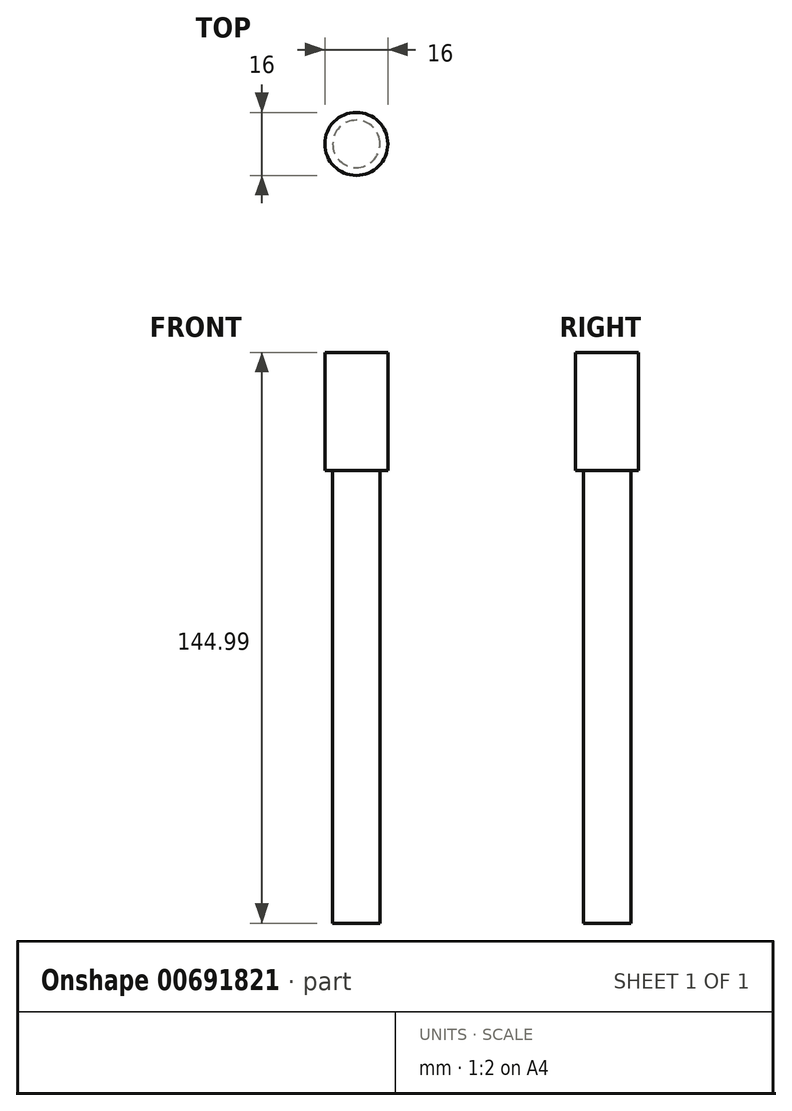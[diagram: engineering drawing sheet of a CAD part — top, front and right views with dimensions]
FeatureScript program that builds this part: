
annotation { "Feature Type Name" : "Feature", "Feature Type Description" : "" }
export const myFeature = defineFeature(function(context is Context, id is Id, definition is map)
    precondition{}
    {
        {
            var Q0;
            Q0=qCreatedBy(makeId("Front.planeOp"),FACE);
            var sketch = newSketch(context, id + "F0", { "sketchPlane" : qUnion([Q0])});
            skLineSegment(sketch, "E0.bottom", {"start": v(6, -72.5) * mm, "end": v(-6, -72.5) * mm});
            skLineSegment(sketch, "E0.top", {"start": v(6, 72.5) * mm, "end": v(-6, 72.5) * mm});
            skLineSegment(sketch, "E0.left", {"start": v(6, -72.5) * mm, "end": v(6, 72.5) * mm});
            skLineSegment(sketch, "E0.right", {"start": v(-6, -72.5) * mm, "end": v(-6, 72.5) * mm});
            skPoint(sketch, "E0.middle", {"position": v(0, 0) * mm});
            skLineSegment(sketch, "E1.bottom", {"start": v(8, 42.5) * mm, "end": v(-8, 42.5) * mm});
            skLineSegment(sketch, "E1.top", {"start": v(8, 72.5) * mm, "end": v(-8, 72.5) * mm});
            skLineSegment(sketch, "E1.left", {"start": v(8, 42.5) * mm, "end": v(8, 72.5) * mm});
            skLineSegment(sketch, "E1.right", {"start": v(-8, 42.5) * mm, "end": v(-8, 72.5) * mm});
            skPoint(sketch, "E1.middle", {"position": v(0, 57.5) * mm});
            skLineSegment(sketch, "E2", {"start": v(0, 72.5) * mm, "end": v(0, -72.5) * mm});
            skSolve(sketch);
        }
        {
            var Q0;
            {var subQ5=sQuery(id+"F0.wireOp",EDGE,"E1.left");Q0=makeQuery(id+"F0.imprint","IMPRINT",FACE,{"disambiguationData":[TD([[makeQuery(id+"F0.imprint","IMPRINT",EDGE,{"derivedFrom":subQ5}),1.0]])]});}
            var Q1;
            {var subQ0=sQuery(id+"F0.wireOp",EDGE,"E1.bottom");var subQ1=sQuery(id+"F0.wireOp",EDGE,"E0.left");var subQ2=makeQuery(id+"F0.imprint","INTERSECT",VERTEX,{"derivedFrom":[subQ1,subQ0]});Q1=makeQuery(id+"F0.imprint","IMPRINT",FACE,{"disambiguationData":[TD([[makeQuery(id+"F0.imprint","IMPRINT",EDGE,{"disambiguationData":[TD([[subQ2,-1.0]])],"derivedFrom":subQ1}),1.0]])]});}
            var Q2;
            {var subQ0=sQuery(id+"F0.wireOp",EDGE,"E0.left");var subQ1=sQuery(id+"F0.wireOp",EDGE,"E0.bottom");var subQ2=makeQuery(id+"F0.imprint","INTERSECT",VERTEX,{"derivedFrom":[subQ1,subQ0]});Q2=makeQuery(id+"F0.imprint","IMPRINT",FACE,{"disambiguationData":[TD([[makeQuery(id+"F0.imprint","IMPRINT",EDGE,{"disambiguationData":[TD([[subQ2,-1.0]])],"derivedFrom":subQ1}),-1.0]])]});}
            var Q3;
            Q3=sQuery(id+"F0.wireOp",EDGE,"E2");
            revolve(context, id + "F1", {"surfaceOperationType" : NewSurfaceOperationType.NEW, "entities" : qUnion([Q0, Q1, Q2]), "axis" : qUnion([Q3]), "revolveType" : RevolveType.FULL});
        }
    });
